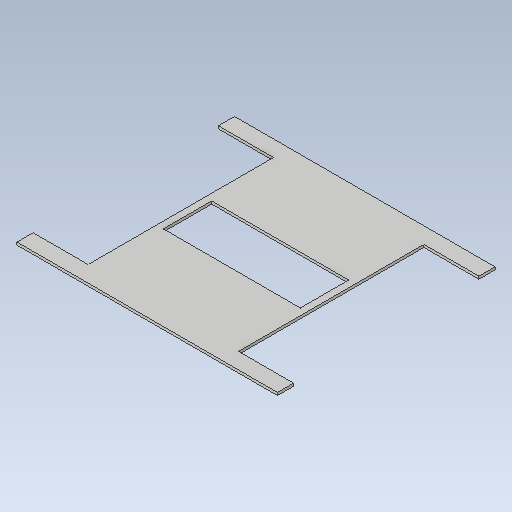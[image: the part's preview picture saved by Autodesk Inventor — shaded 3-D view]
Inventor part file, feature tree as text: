
AUTODESK INVENTOR PART (.ipt)
format: ipt  version: 2020 (Build 240168000, 168)  size: 131,072 bytes
history: native  units: mm
features: extrude x3, sketch x3, other x1
ambient origin geometry x8: Origin, YZ Plane, XZ Plane, XY Plane, X Axis, Y Axis, Z Axis, Center Point
bodies: Body1 (feature_tree)
feature tree (7):
  other  "Bryła1"
  extrude  "Wyciągnięcie proste1"  Depth=81.0mm
  extrude  "Wyciągnięcie proste2"  Depth=56.0mm
  extrude  "Wyciągnięcie proste4"  Depth=28.0mm
  sketch  "Szkic1"
  sketch  "Szkic2"
  sketch  "Szkic3"
